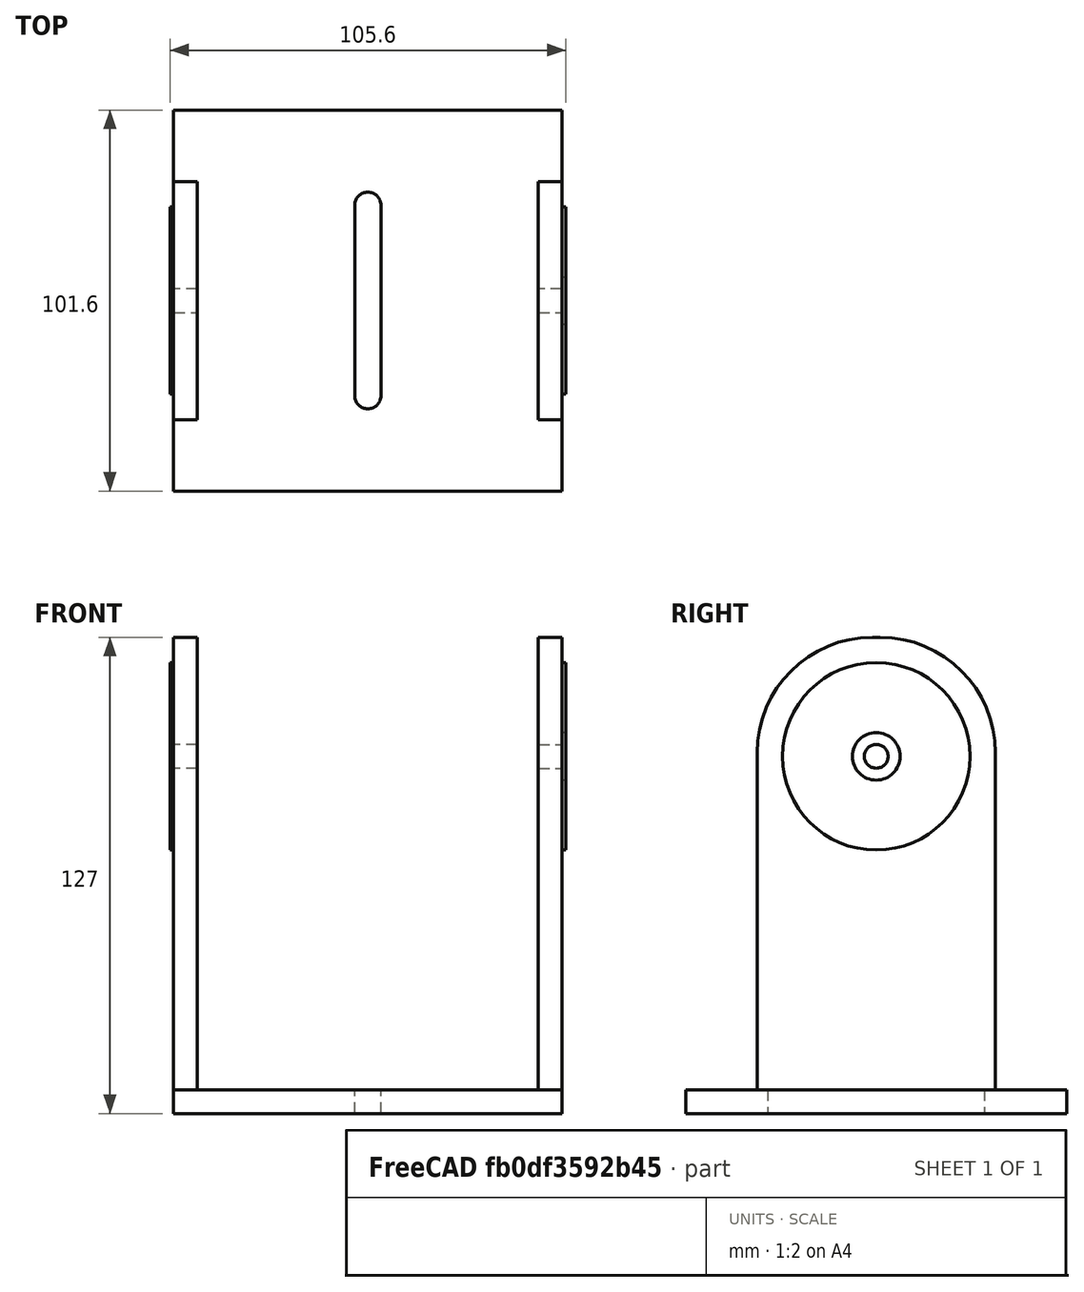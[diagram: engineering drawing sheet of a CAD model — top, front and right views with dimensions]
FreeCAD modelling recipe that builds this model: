
FCSTD DOCUMENT  (FreeCAD 0.19R24291 (Git))
Label: Pivot_Fork
License: All rights reserved
LicenseURL: http://en.wikipedia.org/wiki/All_rights_reserved
objects: TechDraw::DrawViewDimension×10, Sketcher::SketchObject×4, PartDesign::Pad×3, TechDraw::DrawProjGroupItem×3, PartDesign::Body×2, Spreadsheet::Sheet×1, PartDesign::Pocket×1, TechDraw::DrawSVGTemplate×1, PartDesign::Fillet×1, TechDraw::DrawProjGroup×1, PartDesign::FeatureBase×1, TechDraw::DrawPage×1
note: 17 computed .brp shape members not serialized (recipe doc carries the construction recipe); baked Part::Feature solids carry a one-line shape summary decoded from their .brp

FEATURE [Sketcher::SketchObject] Sketch  label="SketchBase"
  FullyConstrained = true
  MapMode = 5
  Support = -> [XY_Plane]
  expr: Constraints[15] = <<Spreadsheet>>.BaseWidth
  expr: Constraints[16] = <<Spreadsheet>>.BaseHeight
  expr: Constraints[14] = <<Spreadsheet>>.SlotWidthForScrew
  expr: Constraints[19] = <<Spreadsheet>>.SlotLengthForScrew
  sketch-geometry (8):
    g0: LineSegment StartX=-51.8 StartY=50.8 StartZ=0 EndX=51.8 EndY=50.8 EndZ=0
    g1: LineSegment StartX=51.8 StartY=50.8 StartZ=0 EndX=51.8 EndY=-50.8 EndZ=0
    g2: LineSegment StartX=51.8 StartY=-50.8 StartZ=0 EndX=-51.8 EndY=-50.8 EndZ=0
    g3: LineSegment StartX=-51.8 StartY=-50.8 StartZ=0 EndX=-51.8 EndY=50.8 EndZ=0
    g4: ArcOfCircle CenterX=3e-16 CenterY=25.4 CenterZ=0 NormalX=0 NormalY=0 NormalZ=1 AngleXU=0 Radius=3.4925 StartAngle=0 EndAngle=3.14159
    g5: ArcOfCircle CenterX=2e-16 CenterY=-25.4 CenterZ=0 NormalX=0 NormalY=0 NormalZ=1 AngleXU=0 Radius=3.4925 StartAngle=3.14159 EndAngle=6.28319
    g6: LineSegment StartX=-3.4925 StartY=25.4 StartZ=0 EndX=-3.4925 EndY=-25.4 EndZ=0
    g7: LineSegment StartX=3.4925 StartY=25.4 StartZ=0 EndX=3.4925 EndY=-25.4 EndZ=0
  constraints (20):
    c: Coincident(g0,g1)
    c: Coincident(g1,g2)
    c: Coincident(g2,g3)
    c: Coincident(g3,g0)
    c: Horizontal(g0)
    c: Horizontal(g2)
    c: Vertical(g1)
    c: Vertical(g3)
    c: Tangent(g4,g7) = 1.5708
    c: Tangent(g4,g6) = -1.5708
    c: Tangent(g6,g5) = -1.5708
    c: Tangent(g7,g5) = 1.5708
    c: Vertical(g6)
    c: Equal(g4,g5)
    c: DistanceX(g4,g4) = 6.985
    c: DistanceX(g0,g0) = 103.6
    c: DistanceY(g1,g1) = 101.6
    c: Symmetric(g0,g1,g-1)
    c: Symmetric(g4,g5,g-1)
    c: DistanceY(g5,g4) = 50.8
FEATURE [PartDesign::Pad] Pad  label="PadBase"
  Direction = (1,1,1)
  Length = 6.35
  Length2 = 100
  Profile = -> Sketch
  Type = 0
  expr: Length = <<Spreadsheet>>.BaseThickness
FEATURE [Spreadsheet::Sheet] Spreadsheet
  cells = A1=Fork PST; C4=Thickness of Pivot width plus Rim Height; C5=Use  76.2 + twice BaseThickness + twice RaisedRimHeight; C6==88.90000000000001mm + 2 * BaseThickness + 2 * PivotPointRaisedRimHeight; A7=BaseWidth; B7(BaseWidth)==C6; A8=BaseHeight; B8(BaseHeight)==4 * 25.4mm; A9=SideHeight; B9(SideHeight)==2.5"; C9="Height" because same direction as base height so Z; A10=BaseThickness; B10(BaseThickness)==0.25 * 25.4mm; A11=SlotWidthForScrew; B11(SlotWidthForScrew)==25.4 / 4 * 1.1mm; C11=Quarter20 with clearance; A12=SlotLengthForScrew; B12(SlotLengthForScrew)==25.4 * 2mm; A13=PivotPointHeight; B13(PivotPointHeight)==3.5"; C13=This "Height" is up from base, so Z.; A14=PivotPointHoleDiameter; B14(PivotPointHoleDiameter)==25.4 * 0.25mm; A15=PivotPointRaisedRimHeight; B15(PivotPointRaisedRimHeight)==1mm; A16=PivotPointRaisedRimOD; B16(PivotPointRaisedRimOD)==50mm
FEATURE [Sketcher::SketchObject] Sketch001  label="SketchForkSide"
  FullyConstrained = true
  MapMode = 5
  Placement = pos=(0,0,6.35) rot=(0,0,1;0rad)
  Support = -> [Pad]
  expr: Constraints[7] = <<Spreadsheet>>.SideHeight
  expr: Constraints[8] = <<Spreadsheet>>.BaseThickness
  expr: Constraints[9] = <<Spreadsheet>>.BaseWidth / 2
  sketch-geometry (4):
    g0: LineSegment StartX=-51.8 StartY=31.75 StartZ=0 EndX=-45.45 EndY=31.75 EndZ=0
    g1: LineSegment StartX=-45.45 StartY=31.75 StartZ=0 EndX=-45.45 EndY=-31.75 EndZ=0
    g2: LineSegment StartX=-45.45 StartY=-31.75 StartZ=0 EndX=-51.8 EndY=-31.75 EndZ=0
    g3: LineSegment StartX=-51.8 StartY=-31.75 StartZ=0 EndX=-51.8 EndY=31.75 EndZ=0
  constraints (11):
    c: Coincident(g0,g1)
    c: Coincident(g1,g2)
    c: Coincident(g2,g3)
    c: Coincident(g3,g0)
    c: Horizontal(g0)
    c: Horizontal(g2)
    c: Vertical(g3)
    c: DistanceY(g3,g3) = 63.5
    c: DistanceX(g0,g0) = 6.35
    c: DistanceX(g0,g-1) = 51.8
    c: Symmetric(g0,g1,g-1)
FEATURE [PartDesign::Pad] Pad001  label="PadForkSide"
  BaseFeature = -> Pad
  Direction = (1,1,1)
  Length = 120.65
  Length2 = 99.9998
  Profile = -> Sketch001
  Type = 0
  expr: Length = <<Spreadsheet>>.PivotPointHeight + 0.5 * <<Spreadsheet>>.SideHeight
FEATURE [Sketcher::SketchObject] Sketch002
  FullyConstrained = true
  MapMode = 5
  Placement = pos=(-51.8,0,0) rot=(0.57735,-0.57735,-0.57735;2.0944rad)
  Support = -> [Pad001]
  expr: Constraints[2] = <<Spreadsheet>>.PivotPointHoleDiameter
  expr: Constraints[1] = <<Spreadsheet>>.PivotPointHeight + <<Spreadsheet>>.BaseThickness
  sketch-geometry (1):
    g0: Circle CenterX=0 CenterY=95.25 CenterZ=0 NormalX=0 NormalY=0 NormalZ=1 AngleXU=0 Radius=3.175
  constraints (3):
    c: PointOnObject(g0,g-2)
    c: DistanceY(g-1,g0) = 95.25
    c: Diameter(g0) = 6.35
FEATURE [PartDesign::Pocket] Pocket  label="PocketForkHole"
  BaseFeature = -> Pad001
  Length = 5
  Length2 = 99.9998
  Profile = -> Sketch002
  Type = 1
FEATURE [Sketcher::SketchObject] Sketch003
  FullyConstrained = true
  MapMode = 5
  Placement = pos=(-51.8,0,0) rot=(0.57735,-0.57735,-0.57735;2.0944rad)
  Support = -> [Pad001]
  expr: Constraints[3] = <<Spreadsheet>>.PivotPointRaisedRimOD
  expr: Constraints[4] = <<Spreadsheet>>.PivotPointHoleDiameter + <<Spreadsheet>>.BaseThickness
  expr: Constraints[2] = <<Spreadsheet>>.PivotPointHeight + <<Spreadsheet>>.BaseThickness
  sketch-geometry (2):
    g0: Circle CenterX=0 CenterY=95.25 CenterZ=0 NormalX=0 NormalY=0 NormalZ=1 AngleXU=0 Radius=25
    g1: Circle CenterX=0 CenterY=95.25 CenterZ=0 NormalX=0 NormalY=0 NormalZ=1 AngleXU=0 Radius=6.35
  constraints (5):
    c: PointOnObject(g0,g-2)
    c: Coincident(g1,g0)
    c: DistanceY(g-1,g0) = 95.25
    c: Diameter(g0) = 50
    c: Diameter(g1) = 12.7
FEATURE [PartDesign::Pad] Pad002  label="PadRimOutside"
  BaseFeature = -> Pocket
  Direction = (1,1,1)
  Length = 1
  Length2 = 100
  Profile = -> Sketch003
  Type = 0
  expr: Length = <<Spreadsheet>>.PivotPointRaisedRimHeight
FEATURE [TechDraw::DrawSVGTemplate] Template
  Height = 304.8
  Orientation = 1
  Width = 457.2
FEATURE [PartDesign::Fillet] Fillet
  Base = -> Pad002 [Edge39,Edge35]
  BaseFeature = -> Pad002
  Radius = 30.75
  SupportTransform = false
  expr: Radius = <<Spreadsheet>>.SideHeight / 2 - 1mm
FEATURE [PartDesign::Body] Body  label="BodyForkLeft"
  Group = -> [Sketch,Pad,Sketch001,Pad001,Sketch002,Pocket,Sketch003,Pad002,Fillet]
  Origin = -> Origin
  Tip = -> Fillet
FEATURE [TechDraw::DrawProjGroupItem] ProjItem  label="Front"
  CoarseView = false
  Direction = (1,0,0)
  Focus = 100
  HardHidden = false
  IsoCount = 0
  IsoHidden = false
  IsoVisible = false
  LockPosition = true
  Perspective = false
  Rotation = 0
  RotationVector = (0,1,0)
  ScaleType = 2
  SeamHidden = false
  SeamVisible = true
  SmoothHidden = false
  SmoothVisible = true
  Source = -> [Body]
  Type = 0
  X = 0
  XDirection = (0,1,0)
  Y = 0
FEATURE [TechDraw::DrawProjGroupItem] ProjItem002  label="Bottom"
  CoarseView = false
  Direction = (0,0,-1)
  Focus = 100
  HardHidden = false
  IsoCount = 0
  IsoHidden = false
  IsoVisible = false
  LockPosition = true
  Perspective = false
  Rotation = 0
  RotationVector = (1,0,0)
  ScaleType = 2
  SeamHidden = false
  SeamVisible = true
  SmoothHidden = false
  SmoothVisible = true
  Source = -> [Body]
  Type = 5
  X = 0
  XDirection = (0,1,0)
  Y = 141.761
FEATURE [TechDraw::DrawViewDimension] Dimension004
  Arbitrary = false
  ArbitraryTolerances = false
  EqualTolerance = true
  FormatSpec = %.3f
  FormatSpecOverTolerance = %+.3f
  FormatSpecUnderTolerance = %+.3f
  Inverted = false
  LockPosition = false
  MeasureType = 1
  OverTolerance = 0
  References2D = -> [ProjItem]
  Rotation = 0
  ScaleType = 2
  TheoreticalExact = false
  Type = 2
  UnderTolerance = 0
  X = 74.5917
  Y = 5.33611
FEATURE [TechDraw::DrawProjGroupItem] ProjItem003  label="FrontTopRight"
  CoarseView = false
  Direction = (0.57735,0.57735,0.57735)
  Focus = 100
  HardHidden = false
  IsoCount = 0
  IsoHidden = false
  IsoVisible = false
  LockPosition = true
  Perspective = false
  Rotation = 0
  RotationVector = (1,0,0)
  ScaleType = 2
  SeamHidden = false
  SeamVisible = true
  SmoothHidden = false
  SmoothVisible = true
  Source = -> [Body]
  Type = 7
  X = 231.771
  XDirection = (-0.707107,0.707107,0)
  Y = 86.5123
FEATURE [TechDraw::DrawProjGroup] ProjGroup
  Anchor = -> ProjItem
  AutoDistribute = true
  LockPosition = false
  ProjectionType = 0
  Rotation = 0
  ScaleType = 2
  Source = -> [Body]
  Views = -> [ProjItem,ProjItem002,ProjItem003]
  X = 85.4014
  Y = 90.7188
  spacingX = 15.0114
  spacingY = 15.0114
FEATURE [PartDesign::FeatureBase] Clone
  BaseFeature = -> Fillet
FEATURE [PartDesign::Body] Body001  label="BodyCloneRighFork"
  BaseFeature = -> Fillet
  Group = -> [Clone]
  Origin = -> Origin001
  Placement = pos=(0,0,0) rot=(0,0,1;3.14159rad)
  Tip = -> Clone
FEATURE [TechDraw::DrawViewDimension] Dimension
  Arbitrary = false
  ArbitraryTolerances = false
  EqualTolerance = true
  FormatSpec = ⌀%.3f
  FormatSpecOverTolerance = %+.3f
  FormatSpecUnderTolerance = %+.3f
  Inverted = false
  LockPosition = false
  MeasureType = 1
  OverTolerance = 0
  References2D = -> [ProjItem]
  Rotation = 0
  ScaleType = 2
  TheoreticalExact = false
  Type = 5
  UnderTolerance = 0
  X = 46.8923
  Y = 64.9278
FEATURE [TechDraw::DrawViewDimension] Dimension005
  Arbitrary = false
  ArbitraryTolerances = false
  EqualTolerance = true
  FormatSpec = ⌀%.3f
  FormatSpecOverTolerance = %+.3f
  FormatSpecUnderTolerance = %+.3f
  Inverted = false
  LockPosition = false
  MeasureType = 1
  OverTolerance = 0
  References2D = -> [ProjItem]
  Rotation = 0
  ScaleType = 2
  TheoreticalExact = false
  Type = 5
  UnderTolerance = 0
  X = 28.8568
  Y = 72.142
FEATURE [TechDraw::DrawViewDimension] Dimension006
  Arbitrary = false
  ArbitraryTolerances = false
  EqualTolerance = true
  FormatSpec = %.3f
  FormatSpecOverTolerance = %+.3f
  FormatSpecUnderTolerance = %+.3f
  Inverted = false
  LockPosition = false
  MeasureType = 1
  OverTolerance = 0
  References2D = -> [ProjItem002]
  Rotation = 0
  ScaleType = 2
  TheoreticalExact = false
  Type = 1
  UnderTolerance = 0
  X = -1.35266
  Y = -59.8669
FEATURE [TechDraw::DrawViewDimension] Dimension007
  Arbitrary = false
  ArbitraryTolerances = false
  EqualTolerance = true
  FormatSpec = %.3f
  FormatSpecOverTolerance = %+.3f
  FormatSpecUnderTolerance = %+.3f
  Inverted = false
  LockPosition = false
  MeasureType = 1
  OverTolerance = 0
  References2D = -> [ProjItem002]
  Rotation = 0
  ScaleType = 2
  TheoreticalExact = false
  Type = 2
  UnderTolerance = 0
  X = 70.6391
  Y = -1.30355
FEATURE [TechDraw::DrawViewDimension] Dimension008
  Arbitrary = false
  ArbitraryTolerances = false
  EqualTolerance = true
  FormatSpec = ⌀%.3f
  FormatSpecOverTolerance = %+.3f
  FormatSpecUnderTolerance = %+.3f
  Inverted = false
  LockPosition = false
  MeasureType = 1
  OverTolerance = 0
  References2D = -> [ProjItem002]
  Rotation = 0
  ScaleType = 2
  TheoreticalExact = false
  Type = 5
  UnderTolerance = 0
  X = 37.4237
  Y = 20.7408
FEATURE [TechDraw::DrawViewDimension] Dimension009
  Arbitrary = false
  ArbitraryTolerances = false
  EqualTolerance = true
  FormatSpec = %.3f
  FormatSpecOverTolerance = %+.3f
  FormatSpecUnderTolerance = %+.3f
  Inverted = false
  LockPosition = false
  MeasureType = 1
  OverTolerance = 0
  References2D = -> [ProjItem002]
  Rotation = 0
  ScaleType = 2
  TheoreticalExact = false
  Type = 1
  UnderTolerance = 0
  X = -1.80355
  Y = 19.3227
FEATURE [TechDraw::DrawViewDimension] Dimension010
  Arbitrary = false
  ArbitraryTolerances = false
  EqualTolerance = true
  FormatSpec = %.3f
  FormatSpecOverTolerance = %+.3f
  FormatSpecUnderTolerance = %+.3f
  Inverted = false
  LockPosition = false
  MeasureType = 1
  OverTolerance = 0
  References2D = -> [ProjItem]
  Rotation = 0
  ScaleType = 2
  TheoreticalExact = false
  Type = 2
  UnderTolerance = 0
  X = -56.0531
  Y = -2.23565
FEATURE [TechDraw::DrawViewDimension] Dimension011
  Arbitrary = false
  ArbitraryTolerances = false
  EqualTolerance = true
  FormatSpec = %.3f
  FormatSpecOverTolerance = %+.3f
  FormatSpecUnderTolerance = %+.3f
  Inverted = false
  LockPosition = false
  MeasureType = 1
  OverTolerance = 0
  References2D = -> [ProjItem]
  Rotation = 0
  ScaleType = 2
  TheoreticalExact = false
  Type = 2
  UnderTolerance = 0
  X = 58.6279
  Y = -38.4069
FEATURE [TechDraw::DrawViewDimension] Dimension012
  Arbitrary = false
  ArbitraryTolerances = false
  EqualTolerance = true
  FormatSpec = %.3f
  FormatSpecOverTolerance = %+.3f
  FormatSpecUnderTolerance = %+.3f
  Inverted = false
  LockPosition = false
  MeasureType = 1
  OverTolerance = 0
  References2D = -> [ProjItem]
  Rotation = 0
  ScaleType = 2
  TheoreticalExact = false
  Type = 1
  UnderTolerance = 0
  X = 0.901775
  Y = -68.9107
FEATURE [TechDraw::DrawPage] Page
  KeepUpdated = true
  NextBalloonIndex = 1
  ProjectionType = 0
  Template = -> Template
  Views = -> [ProjGroup,Dimension004,Dimension,Dimension005,Dimension006,Dimension007,Dimension008,Dimension009,Dimension010,Dimension011,Dimension012]
